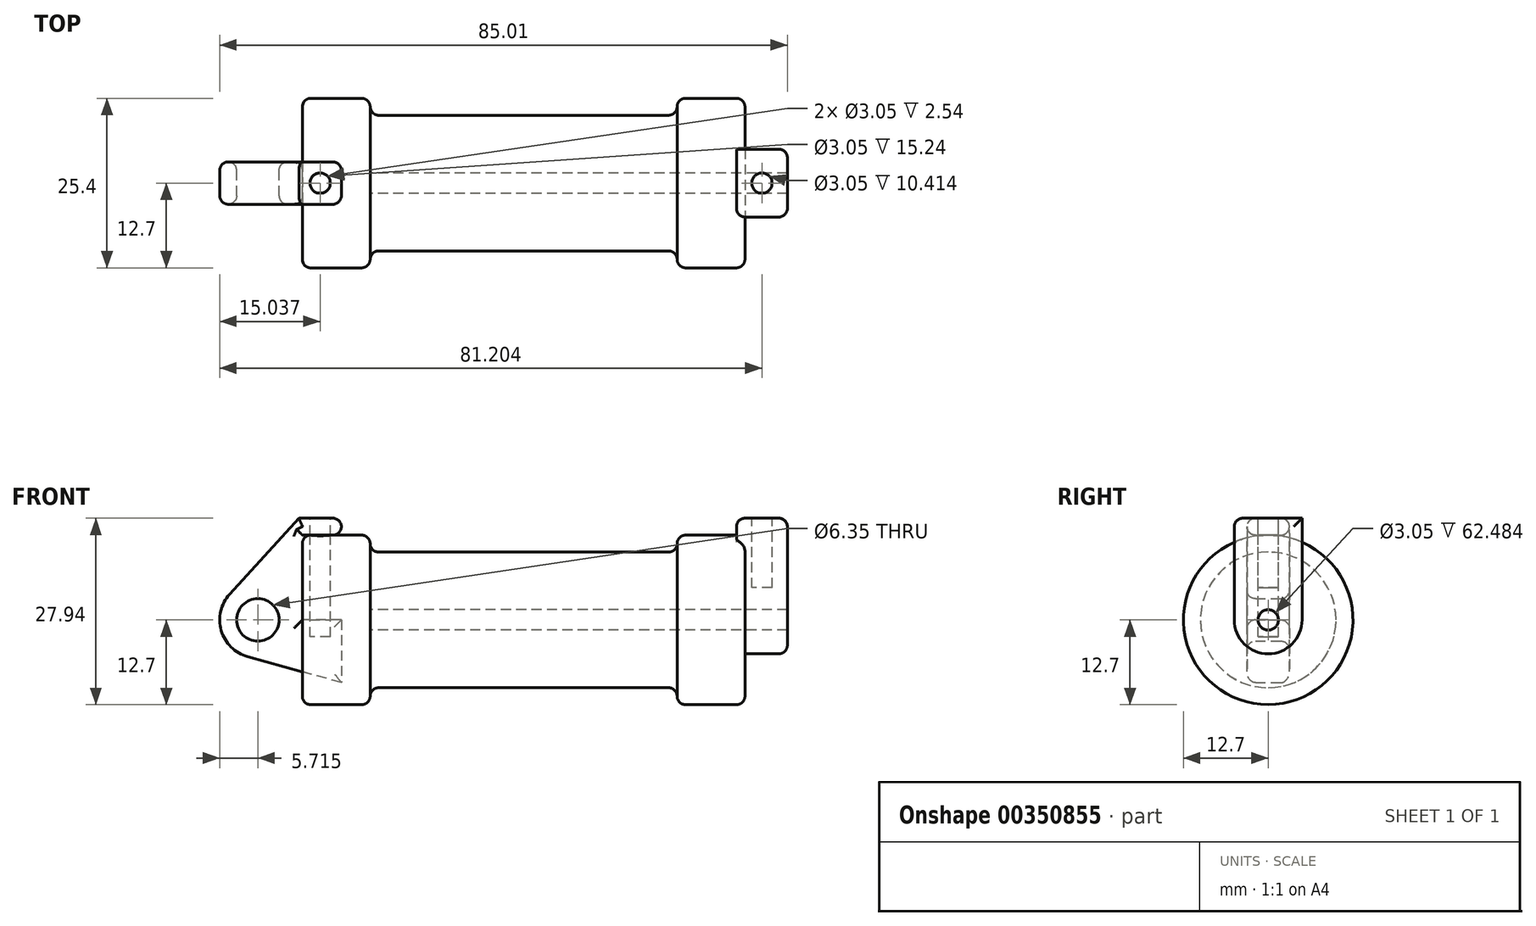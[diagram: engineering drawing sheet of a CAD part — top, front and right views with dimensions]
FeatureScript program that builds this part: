
annotation { "Feature Type Name" : "Feature", "Feature Type Description" : "" }
export const myFeature = defineFeature(function(context is Context, id is Id, definition is map)
    precondition{}
    {
        {
            var Q0;
            Q0=qCreatedBy(makeId("Front.planeOp"),FACE);
            var sketch = newSketch(context, id + "F0", { "sketchPlane" : qUnion([Q0])});
            skLineSegment(sketch, "E0", {"start": v(0, 0) * mm, "end": v(0, 12.7) * mm});
            skLineSegment(sketch, "E1", {"start": v(0, 12.7) * mm, "end": v(10.16, 12.7) * mm});
            skLineSegment(sketch, "E2", {"start": v(10.16, 12.7) * mm, "end": v(10.16, 10.16) * mm});
            skLineSegment(sketch, "E3", {"start": v(10.16, 10.16) * mm, "end": v(56.13, 10.16) * mm});
            skLineSegment(sketch, "E4", {"start": v(56.13, 10.16) * mm, "end": v(56.13, 12.7) * mm});
            skLineSegment(sketch, "E5", {"start": v(56.13, 12.7) * mm, "end": v(66.3, 12.7) * mm});
            skLineSegment(sketch, "E6", {"start": v(66.3, 12.7) * mm, "end": v(66.3, 0) * mm});
            skLineSegment(sketch, "E7", {"start": v(66.3, 0) * mm, "end": v(0, 0) * mm});
            skLineSegment(sketch, "E8", {"start": v(5.84, 15.24) * mm, "end": v(-0.5, 15.24) * mm});
            skLineSegment(sketch, "E9", {"start": v(-0.5, 15.24) * mm, "end": v(-10.88, 3.85) * mm});
            skLineSegment(sketch, "E10", {"start": v(0, 0) * mm, "end": v(-6.65, 0) * mm});
            skCircle(sketch, "E11", {"center": v(-6.65, 0) * mm, "radius": 5.72 * mm});
            skCircle(sketch, "E12", {"center": v(-6.65, 0) * mm, "radius": 3.18 * mm});
            skLineSegment(sketch, "E13", {"start": v(5.84, 15.24) * mm, "end": v(5.84, -9.4) * mm});
            skLineSegment(sketch, "E14", {"start": v(5.84, -9.4) * mm, "end": v(-8.18, -5.5) * mm});
            skSolve(sketch);
        }
        {
            var Q0;
            {var subQ0=sQuery(id+"F0.wireOp",EDGE,"E2");Q0=makeQuery(id+"F0.imprint","IMPRINT",FACE,{"disambiguationData":[TD([[makeQuery(id+"F0.imprint","IMPRINT",EDGE,{"derivedFrom":subQ0}),-1.0]])]});}
            var Q1;
            {var subQ0=sQuery(id+"F0.wireOp",EDGE,"E0");Q1=makeQuery(id+"F0.imprint","IMPRINT",FACE,{"disambiguationData":[TD([[makeQuery(id+"F0.imprint","IMPRINT",EDGE,{"derivedFrom":subQ0}),-1.0]])]});}
            var Q2;
            Q2=sQuery(id+"F0.wireOp",EDGE,"E7");
            revolve(context, id + "F1", {"entities" : qUnion([Q0, Q1]), "axis" : qUnion([Q2]), "revolveType" : RevolveType.FULL});
        }
        {
            var Q0;
            {var subQ1=sQuery(id+"F0.wireOp",EDGE,"E0");Q0=makeQuery(id+"F0.imprint","IMPRINT",FACE,{"disambiguationData":[TD([[makeQuery(id+"F0.imprint","IMPRINT",EDGE,{"derivedFrom":subQ1}),1.0]])]});}
            var Q1;
            {var subQ5=sQuery(id+"F0.wireOp",EDGE,"E12");Q1=makeQuery(id+"F0.imprint","IMPRINT",FACE,{"disambiguationData":[TD([[makeQuery(id+"F0.imprint","IMPRINT",EDGE,{"derivedFrom":subQ5}),-1.0]])]});}
            var Q2;
            {var subQ0=sQuery(id+"F0.wireOp",EDGE,"E14");Q2=makeQuery(id+"F0.imprint","IMPRINT",FACE,{"disambiguationData":[TD([[makeQuery(id+"F0.imprint","IMPRINT",EDGE,{"derivedFrom":subQ0}),-1.0]])]});}
            extrude(context, id + "F2", {"entities" : qUnion([Q0, Q1, Q2]), "endBound" : BoundingType.SYMMETRIC, "depth" : 6.35 * mm});
        }
        {
            var Q0;
            Q0=makeQuery(id+"F1.opRevolve","SWEPT_FACE",FACE,{"disambiguationData":[OSD([sQuery(id+"F0.wireOp",EDGE,"E6")])]});
            var sketch = newSketch(context, id + "F3", { "sketchPlane" : qUnion([Q0])});
            skCircle(sketch, "E15", {"center": v(0, 0) * mm, "radius": 1.52 * mm});
            skCircle(sketch, "E16", {"center": v(0, 0) * mm, "radius": 5.08 * mm});
            skLineSegment(sketch, "E17", {"start": v(-5.08, 0) * mm, "end": v(-5.08, 15.24) * mm});
            skLineSegment(sketch, "E18", {"start": v(5.08, 0) * mm, "end": v(5.08, 15.24) * mm});
            skLineSegment(sketch, "E19", {"start": v(5.08, 15.24) * mm, "end": v(-5.08, 15.24) * mm});
            skSolve(sketch);
        }
        {
            var Q0;
            {var subQ0=sQuery(id+"F3.wireOp",EDGE,"E19");Q0=makeQuery(id+"F3.imprint","IMPRINT",FACE,{"disambiguationData":[TD([[makeQuery(id+"F3.imprint","IMPRINT",EDGE,{"derivedFrom":subQ0}),1.0]])]});}
            var Q1;
            {var subQ0=sQuery(id+"F3.wireOp",EDGE,"E17");var subQ1=sQuery(id+"F3.wireOp",EDGE,"E16");var subQ2=makeQuery(id+"F3.imprint","INTERSECT",VERTEX,{"derivedFrom":[subQ1,subQ0]});Q1=makeQuery(id+"F3.imprint","IMPRINT",FACE,{"disambiguationData":[TD([[makeQuery(id+"F3.imprint","IMPRINT",EDGE,{"disambiguationData":[TD([[subQ2,1.0]])],"derivedFrom":subQ1}),-1.0]])]});}
            var Q2;
            Q2=makeQuery(id+"F3.imprint","IMPRINT",FACE,{"disambiguationData":[TD([[makeQuery(id+"F3.imprint","IMPRINT",EDGE,{"derivedFrom":sQuery(id+"F3.wireOp",EDGE,"E15")}),-1.0]])]});
            extrude(context, id + "F4", {"entities" : qUnion([Q0, Q1, Q2]), "operationType" : NewBodyOperationType.ADD, "depth" : 6.35 * mm});
        }
        {
            var Q0;
            Q0=makeQuery(id+"F4.opExtrude","CAP_FACE",FACE,{"disambiguationData":[OSD([sQuery(id+"F3.wireOp",EDGE,"E15"),sQuery(id+"F3.wireOp",EDGE,"E16"),sQuery(id+"F3.wireOp",EDGE,"E17"),sQuery(id+"F3.wireOp",EDGE,"E18"),sQuery(id+"F3.wireOp",EDGE,"E19")])],"isStart":true});
            extrude(context, id + "F5", {"entities" : qUnion([Q0]), "operationType" : NewBodyOperationType.ADD, "depth" : 1.27 * mm});
        }
        {
            var Q0;
            Q0=makeQuery(id+"F4.boolean.opBoolean","SPLIT",FACE,{"disambiguationData":[TD([makeQuery(id+"F4.opExtrude","SWEPT_FACE",FACE,{"disambiguationData":[OSD([sQuery(id+"F3.wireOp",EDGE,"E15")])]})])],"derivedFrom":makeQuery(id+"F1.opRevolve","SWEPT_FACE",FACE,{"disambiguationData":[OSD([sQuery(id+"F0.wireOp",EDGE,"E6")])]})});
            var Q1;
            Q1=makeQuery(id+"F1.opRevolve","SWEPT_FACE",FACE,{"disambiguationData":[OSD([sQuery(id+"F0.wireOp",EDGE,"E2")])]});
            extrude(context, id + "F6", {"entities" : qUnion([Q0]), "operationType" : NewBodyOperationType.REMOVE, "endBound" : BoundingType.UP_TO_SURFACE, "oppositeDirection" : true, "endBoundEntityFace" : qUnion([Q1]), "depth" : 25.4 * mm});
        }
        {
            var Q0;
            Q0=makeQuery(id+"F2.opExtrude","SWEPT_FACE",FACE,{"disambiguationData":[OSD([sQuery(id+"F0.wireOp",EDGE,"E8")])]});
            var sketch = newSketch(context, id + "F7", { "sketchPlane" : qUnion([Q0])});
            skCircle(sketch, "E20", {"center": v(2.67, 0) * mm, "radius": 1.52 * mm});
            skSolve(sketch);
        }
        {
            var Q0;
            Q0=makeQuery(id+"F7.imprint","IMPRINT",FACE,{"disambiguationData":[TD([[makeQuery(id+"F7.imprint","IMPRINT",EDGE,{"derivedFrom":sQuery(id+"F7.wireOp",EDGE,"E20")}),1.0]])]});
            extrude(context, id + "F8", {"entities" : qUnion([Q0]), "operationType" : NewBodyOperationType.REMOVE, "oppositeDirection" : true, "depth" : 17.78 * mm});
        }
        {
            var Q0;
            {var subQ0=sQuery(id+"F3.wireOp",EDGE,"E19");Q0=makeQuery(id+"F5.boolean.opBoolean","MERGE",FACE,{"derivedFrom":[makeQuery(id+"F4.opExtrude","SWEPT_FACE",FACE,{"disambiguationData":[OSD([subQ0])]}),makeQuery(id+"F5.opExtrude","SWEPT_FACE",FACE,{"disambiguationData":[OSD([subQ0])]})]});}
            var sketch = newSketch(context, id + "F9", { "sketchPlane" : qUnion([Q0])});
            skLineSegment(sketch, "E21", {"start": v(65.02, 0) * mm, "end": v(72.64, 0) * mm});
            skCircle(sketch, "E22", {"center": v(68.83, 0) * mm, "radius": 1.52 * mm});
            skSolve(sketch);
        }
        {
            var Q0;
            {var subQ0=sQuery(id+"F9.wireOp",EDGE,"E22");var subQ1=sQuery(id+"F9.wireOp",EDGE,"E21");var subQ2=makeQuery(id+"F9.imprint","INTERSECT",VERTEX,{"disambiguationData":[OD(0.0)],"derivedFrom":[subQ1,subQ0]});Q0=makeQuery(id+"F9.imprint","IMPRINT",FACE,{"disambiguationData":[TD([[makeQuery(id+"F9.imprint","IMPRINT",EDGE,{"disambiguationData":[TD([[subQ2,-1.0]])],"derivedFrom":subQ1}),-1.0]])]});}
            var Q1;
            {var subQ0=sQuery(id+"F9.wireOp",EDGE,"E22");var subQ1=sQuery(id+"F9.wireOp",EDGE,"E21");var subQ2=makeQuery(id+"F9.imprint","INTERSECT",VERTEX,{"disambiguationData":[OD(0.0)],"derivedFrom":[subQ1,subQ0]});Q1=makeQuery(id+"F9.imprint","IMPRINT",FACE,{"disambiguationData":[TD([[makeQuery(id+"F9.imprint","IMPRINT",EDGE,{"disambiguationData":[TD([[subQ2,-1.0]])],"derivedFrom":subQ1}),1.0]])]});}
            extrude(context, id + "F10", {"entities" : qUnion([Q0, Q1]), "operationType" : NewBodyOperationType.REMOVE, "oppositeDirection" : true, "depth" : 10.4 * mm});
        }
        {
            var Q0;
            Q0=makeQuery(id+"F1.opRevolve","SWEPT_EDGE",EDGE,{"disambiguationData":[OSD([sQuery(id+"F0.wireOp",EDGE,"E1"),sQuery(id+"F0.wireOp",EDGE,"E2")])]});
            var Q1;
            Q1=makeQuery(id+"F1.opRevolve","SWEPT_EDGE",EDGE,{"disambiguationData":[OSD([sQuery(id+"F0.wireOp",EDGE,"E0"),sQuery(id+"F0.wireOp",EDGE,"E1")])]});
            var Q2;
            {var subQ0=sQuery(id+"F0.wireOp",EDGE,"E5");var subQ1=sQuery(id+"F0.wireOp",EDGE,"E6");Q2=makeQuery(id+"F4.boolean.opBoolean","SPLIT",EDGE,{"disambiguationData":[topologyDisambiguationEdgeConnected([makeQuery(id+"F1.opRevolve","SWEPT_FACE",FACE,{"disambiguationData":[OSD([subQ1])]})])],"derivedFrom":makeQuery(id+"F1.opRevolve","SWEPT_EDGE",EDGE,{"disambiguationData":[OSD([subQ0,subQ1])]})});}
            var Q3;
            Q3=makeQuery(id+"F1.opRevolve","SWEPT_EDGE",EDGE,{"disambiguationData":[OSD([sQuery(id+"F0.wireOp",EDGE,"E4"),sQuery(id+"F0.wireOp",EDGE,"E5")])]});
            var Q4;
            Q4=makeQuery(id+"F1.opRevolve","SWEPT_EDGE",EDGE,{"disambiguationData":[OSD([sQuery(id+"F0.wireOp",EDGE,"E2"),sQuery(id+"F0.wireOp",EDGE,"E3")])]});
            var Q5;
            Q5=makeQuery(id+"F1.opRevolve","SWEPT_EDGE",EDGE,{"disambiguationData":[OSD([sQuery(id+"F0.wireOp",EDGE,"E3"),sQuery(id+"F0.wireOp",EDGE,"E4")])]});
            fillet(context, id + "F11", {"entities" : qUnion([Q0, Q1, Q2, Q3, Q4, Q5]), "radius" : 1.27 * mm, "tangentPropagation" : true, "allowEdgeOverflow" : false});
        }
        {
            var Q0;
            Q0=makeQuery(id+"F2.opExtrude","CAP_FACE",FACE,{"disambiguationData":[OSD([sQuery(id+"F0.wireOp",EDGE,"E0"),sQuery(id+"F0.wireOp",EDGE,"E1"),sQuery(id+"F0.wireOp",EDGE,"E7"),sQuery(id+"F0.wireOp",EDGE,"E8"),sQuery(id+"F0.wireOp",EDGE,"E9"),sQuery(id+"F0.wireOp",EDGE,"E11"),sQuery(id+"F0.wireOp",EDGE,"E12"),sQuery(id+"F0.wireOp",EDGE,"E13"),sQuery(id+"F0.wireOp",EDGE,"E14")])],"isStart":false});
            var Q1;
            Q1=makeQuery(id+"F2.opExtrude","CAP_FACE",FACE,{"disambiguationData":[OSD([sQuery(id+"F0.wireOp",EDGE,"E0"),sQuery(id+"F0.wireOp",EDGE,"E1"),sQuery(id+"F0.wireOp",EDGE,"E7"),sQuery(id+"F0.wireOp",EDGE,"E8"),sQuery(id+"F0.wireOp",EDGE,"E9"),sQuery(id+"F0.wireOp",EDGE,"E11"),sQuery(id+"F0.wireOp",EDGE,"E12"),sQuery(id+"F0.wireOp",EDGE,"E13"),sQuery(id+"F0.wireOp",EDGE,"E14")])],"isStart":true});
            var Q2;
            {var subQ0=sQuery(id+"F0.wireOp",EDGE,"E13");Q2=makeQuery(id+"F2.opExtrude","SWEPT_FACE",FACE,{"disambiguationData":[OSD([subQ0]),TDD([makeQuery(id+"F0.imprint","IMPRINT",EDGE,{"disambiguationData":[TD([[makeQuery(id+"F0.imprint","INTERSECT",VERTEX,{"derivedFrom":[sQuery(id+"F0.wireOp",EDGE,"E8"),subQ0]}),-1.0]])],"derivedFrom":subQ0})])]});}
            fillet(context, id + "F12", {"entities" : qUnion([Q0, Q1, Q2]), "radius" : 1.27 * mm, "tangentPropagation" : true, "allowEdgeOverflow" : false});
        }
        {
            var Q0;
            Q0=makeQuery(id+"F4.opExtrude","CAP_EDGE",EDGE,{"disambiguationData":[OSD([sQuery(id+"F3.wireOp",EDGE,"E17")])],"isStart":false});
            var Q1;
            {var subQ0=sQuery(id+"F3.wireOp",EDGE,"E19");var subQ1=sQuery(id+"F3.wireOp",EDGE,"E17");Q1=makeQuery(id+"F5.boolean.opBoolean","MERGE",EDGE,{"derivedFrom":[makeQuery(id+"F4.opExtrude","SWEPT_EDGE",EDGE,{"disambiguationData":[OSD([subQ1,subQ0])]}),makeQuery(id+"F5.opExtrude","SWEPT_EDGE",EDGE,{"disambiguationData":[OSD([subQ1,subQ0])]})]});}
            var Q2;
            Q2=makeQuery(id+"F5.opExtrude","CAP_EDGE",EDGE,{"disambiguationData":[OSD([sQuery(id+"F3.wireOp",EDGE,"E17")])],"isStart":false});
            var Q3;
            Q3=makeQuery(id+"F4.opExtrude","SWEPT_EDGE",EDGE,{"disambiguationData":[OSD([sQuery(id+"F3.wireOp",EDGE,"E16"),sQuery(id+"F3.wireOp",EDGE,"E17")])]});
            var Q4;
            Q4=makeQuery(id+"F4.opExtrude","CAP_EDGE",EDGE,{"disambiguationData":[OSD([sQuery(id+"F3.wireOp",EDGE,"E16")])],"isStart":false});
            var Q5;
            Q5=makeQuery(id+"F4.opExtrude","CAP_EDGE",EDGE,{"disambiguationData":[OSD([sQuery(id+"F3.wireOp",EDGE,"E18")])],"isStart":false});
            var Q6;
            Q6=makeQuery(id+"F4.opExtrude","CAP_EDGE",EDGE,{"disambiguationData":[OSD([sQuery(id+"F3.wireOp",EDGE,"E19")])],"isStart":false});
            var Q7;
            Q7=makeQuery(id+"F5.opExtrude","CAP_EDGE",EDGE,{"disambiguationData":[OSD([sQuery(id+"F3.wireOp",EDGE,"E19")])],"isStart":false});
            fillet(context, id + "F13", {"entities" : qUnion([Q0, Q1, Q2, Q3, Q4, Q5, Q6, Q7]), "radius" : 1.27 * mm, "tangentPropagation" : true, "allowEdgeOverflow" : false});
        }
    });
